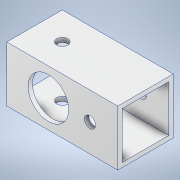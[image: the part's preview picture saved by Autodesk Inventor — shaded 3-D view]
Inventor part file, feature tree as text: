
AUTODESK INVENTOR PART (.ipt)
format: ipt  version: 2020.3 (Build 243373000, 373)  size: 141,312 bytes
history: native  units: mm
features: sketch x4, hole x3, other x1, extrude x1
ambient origin geometry x8: Origin, YZ Plane, XZ Plane, XY Plane, X Axis, Y Axis, Z Axis, Center Point
bodies: Body1 (feature_tree)
feature tree (9):
  other  "ソリッド1"
  extrude  "押し出し1"  Depth=15.0mm
  sketch  "スケッチ2"
  sketch  "スケッチ3"
  hole  "穴1"  [1 undecoded]
  hole  "穴2"  [1 undecoded]
  hole  "穴3"  [1 undecoded]
  sketch  "スケッチ1"
  sketch  "スケッチ4"
note: 3 required parameter values undecoded (feature->parameter linkage not recoverable at this tier; creation-order binding heuristic only, values carry confidence <= 0.55)
